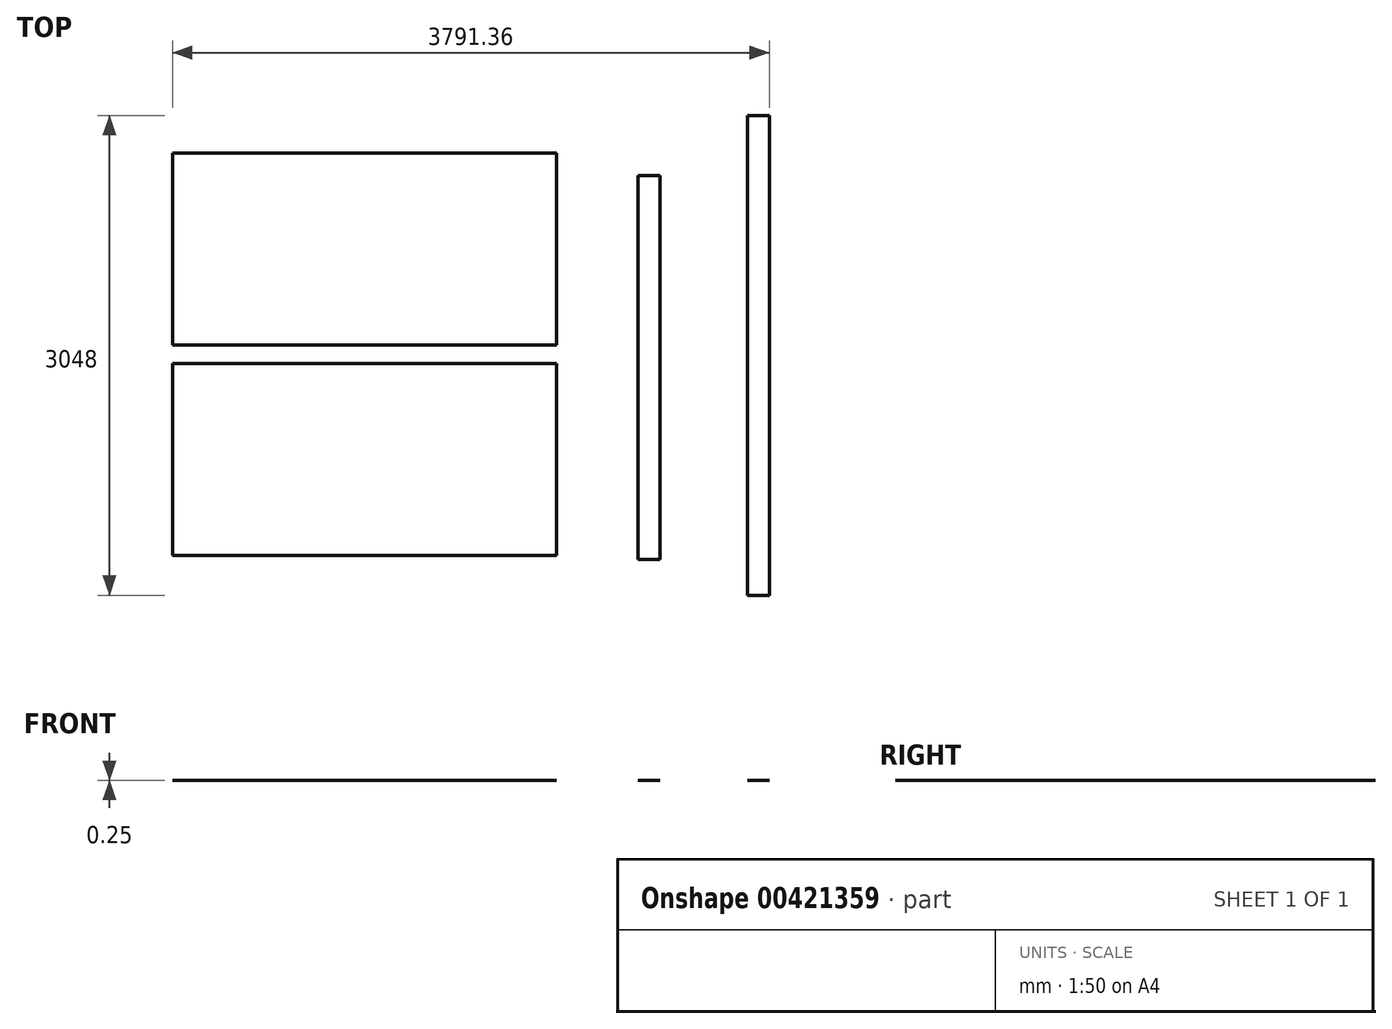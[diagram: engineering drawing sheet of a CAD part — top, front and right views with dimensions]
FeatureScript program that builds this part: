
annotation { "Feature Type Name" : "Feature", "Feature Type Description" : "" }
export const myFeature = defineFeature(function(context is Context, id is Id, definition is map)
    precondition{}
    {
        {
            var Q0;
            Q0=qCreatedBy(makeId("Top.planeOp"),FACE);
            var sketch = newSketch(context, id + "F0", { "sketchPlane" : qUnion([Q0])});
            skLineSegment(sketch, "E0.bottom", {"start": v(-2389.78, 1274.9) * mm, "end": v(48.62, 1274.9) * mm});
            skLineSegment(sketch, "E0.top", {"start": v(-2389.78, 55.7) * mm, "end": v(48.62, 55.7) * mm});
            skLineSegment(sketch, "E0.left", {"start": v(-2389.78, 1274.9) * mm, "end": v(-2389.78, 55.7) * mm});
            skLineSegment(sketch, "E0.right", {"start": v(48.62, 1274.9) * mm, "end": v(48.62, 55.7) * mm});
            skLineSegment(sketch, "E1.bottom", {"start": v(-2389.78, -62.08) * mm, "end": v(48.62, -62.08) * mm});
            skLineSegment(sketch, "E1.top", {"start": v(-2389.78, -1281.28) * mm, "end": v(48.62, -1281.28) * mm});
            skLineSegment(sketch, "E1.left", {"start": v(-2389.78, -62.08) * mm, "end": v(-2389.78, -1281.28) * mm});
            skLineSegment(sketch, "E1.right", {"start": v(48.62, -62.08) * mm, "end": v(48.62, -1281.28) * mm});
            skLineSegment(sketch, "E2", {"start": v(-2389.78, 1014.55) * mm, "end": v(-1773.83, 1014.55) * mm});
            skLineSegment(sketch, "E3", {"start": v(-1773.83, 1014.55) * mm, "end": v(-1773.83, 55.7) * mm});
            skLineSegment(sketch, "E4", {"start": v(-1773.83, 1014.55) * mm, "end": v(-1157.88, 1014.55) * mm});
            skLineSegment(sketch, "E5", {"start": v(-1157.88, 1014.55) * mm, "end": v(-1157.88, 55.7) * mm});
            skLineSegment(sketch, "E6", {"start": v(48.62, 1014.55) * mm, "end": v(-878.48, 1014.55) * mm});
            skLineSegment(sketch, "E7", {"start": v(-878.48, 1014.55) * mm, "end": v(-878.48, 55.7) * mm});
            skLineSegment(sketch, "E8", {"start": v(-1119.78, 1274.9) * mm, "end": v(-1119.78, 55.7) * mm, "construction": true});
            skLineSegment(sketch, "E9", {"start": v(-2389.78, 1033.6) * mm, "end": v(48.62, 1033.6) * mm, "construction": true});
            skLineSegment(sketch, "E10", {"start": v(-2389.78, -379.58) * mm, "end": v(-1773.83, -379.58) * mm});
            skLineSegment(sketch, "E11", {"start": v(-1773.83, -379.58) * mm, "end": v(-1773.83, -1281.28) * mm});
            skLineSegment(sketch, "E12", {"start": v(-1773.83, -379.58) * mm, "end": v(-1157.88, -379.58) * mm});
            skLineSegment(sketch, "E13", {"start": v(-1157.88, -379.58) * mm, "end": v(-1157.88, -1281.28) * mm});
            skLineSegment(sketch, "E14", {"start": v(48.62, -379.58) * mm, "end": v(-884.83, -379.58) * mm});
            skLineSegment(sketch, "E15", {"start": v(-884.83, -379.58) * mm, "end": v(-884.83, -1281.28) * mm});
            skLineSegment(sketch, "E16", {"start": v(-2389.78, -303.38) * mm, "end": v(48.62, -303.38) * mm, "construction": true});
            skLineSegment(sketch, "E17", {"start": v(-1119.78, -62.08) * mm, "end": v(-1119.78, -1281.28) * mm, "construction": true});
            skLineSegment(sketch, "E18.bottom", {"start": v(568.74, 1134.52) * mm, "end": v(708.44, 1134.52) * mm});
            skLineSegment(sketch, "E18.top", {"start": v(568.74, -1303.88) * mm, "end": v(708.44, -1303.88) * mm});
            skLineSegment(sketch, "E18.left", {"start": v(568.74, 1134.52) * mm, "end": v(568.74, -1303.88) * mm});
            skLineSegment(sketch, "E18.right", {"start": v(708.44, 1134.52) * mm, "end": v(708.44, -1303.88) * mm});
            skLineSegment(sketch, "E19", {"start": v(568.74, 569.37) * mm, "end": v(708.44, 569.37) * mm});
            skLineSegment(sketch, "E20", {"start": v(568.74, 4.22) * mm, "end": v(708.44, 4.22) * mm});
            skLineSegment(sketch, "E21", {"start": v(568.74, -560.93) * mm, "end": v(708.44, -560.93) * mm});
            skLineSegment(sketch, "E22", {"start": v(568.74, -1126.08) * mm, "end": v(708.44, -1126.08) * mm});
            skLineSegment(sketch, "E23.bottom", {"start": v(1261.88, 1514.66) * mm, "end": v(1401.58, 1514.66) * mm});
            skLineSegment(sketch, "E23.top", {"start": v(1261.88, -1533.34) * mm, "end": v(1401.58, -1533.34) * mm});
            skLineSegment(sketch, "E23.left", {"start": v(1261.88, 1514.66) * mm, "end": v(1261.88, -1533.34) * mm});
            skLineSegment(sketch, "E23.right", {"start": v(1401.58, 1514.66) * mm, "end": v(1401.58, -1533.34) * mm});
            skLineSegment(sketch, "E24", {"start": v(1261.88, 1070.16) * mm, "end": v(1401.58, 1070.16) * mm});
            skLineSegment(sketch, "E25", {"start": v(1261.88, 625.66) * mm, "end": v(1401.58, 625.66) * mm});
            skLineSegment(sketch, "E26", {"start": v(1261.88, -307.8) * mm, "end": v(1401.58, -307.8) * mm});
            skLineSegment(sketch, "E27", {"start": v(1261.88, -1241.24) * mm, "end": v(1401.58, -1241.24) * mm});
            skSolve(sketch);
        }
        {
            var Q0;
            Q0 = qSketchRegion(id + "F0", true);
            extrude(context, id + "F1", {"entities" : qUnion([Q0]), "depth" : 0.25 * mm});
        }
    });
